# Revit family: PRD_FrankeWS_UrnlFlshngVlvs_SelfClosingUrinalFlushValve_AQRM460
name_source: partatom
category: Plumbing Fixtures
revit_build: Autodesk Revit 2018 (Build: 20190510_1515(x64)
units: mm (PartAtom-declared; Revit-internal decimal feet)

## family parameters
Always vertical = Yes
Cut with Voids When Loaded = No
OmniClass Number = 23.45.05.14.99
OmniClass Title = Other Sanitary Washing Plumbing Fixtures
Part Type = Normal
Room Calculation Point = No
Round Connector Dimension = Use Diameter
Shared = No
Work Plane-Based = No

## types (1)
- AQRM460
    AssetType = Fixed
    BIMObjectName = PRD_AR_UrinalFlushingValves_SelfClosingUrinalFlushValve_AQRM460
    Category = Pr_40_20_93_79, Urinal flushing valves
    Color = Chrome
    Description = AQUALINE urinal flush valve DN 15 for surface installation, flushing quantity and volume flow adjustable, with lockable water quantity regulator, inlet pipe and connector, polished chromium-plated brass, push cap and screw fitting in chromium-plated plastic.
    DurationUnit = year
    FlushValveMaterial = PRD_AR_ChromatedBrass_HighPolished
    FlushingRate = 0.0 L/s
    GrossWeight = 0.65 kg
    HasIntegralShutOffDevice = Yes
    IfcExportAs = IfcValveType
    IfcExportType = FLUSHING
    IsHighPressure = No
    Manufacturer = KWC Group AG
    ManufacturerName = KWC Group AG
    ManufacturerURL = www.kwc.com
    Model = AQRM460
    ModelNumber = 2000065995
    ModelReference = AQRM460
    NBSDescription = Urinal flushing valves
    NBSReference = 45-35-70/355
    Name = Urinal flush valve AQRM460
    NetWeight = 0.60 kg
    NominalHeight = 0 mm  [stored 0 ft]
    NominalLength = 0 mm  [stored 0 ft]
    NominalWidth = 0 mm  [stored 0 ft]
    OperatingControl = Push
    ProductInformation = https://pim.kwc.com
    URL = www.kwc.com
    Uniclass2015Code = Pr_40_20_93_79
    Uniclass2015Title = Urinal flushing valves
    Uniclass2015Version = Products v1.7
    Version = 1
    WarrantyDurationUnit = year

note: [stored X ft] marks values corroborated as IEEE doubles in the binary element streams (Revit-internal decimal feet)

## geometry (parser evidence)
native form markers: Sweep x3
no freeform markers — native parametric forms only
